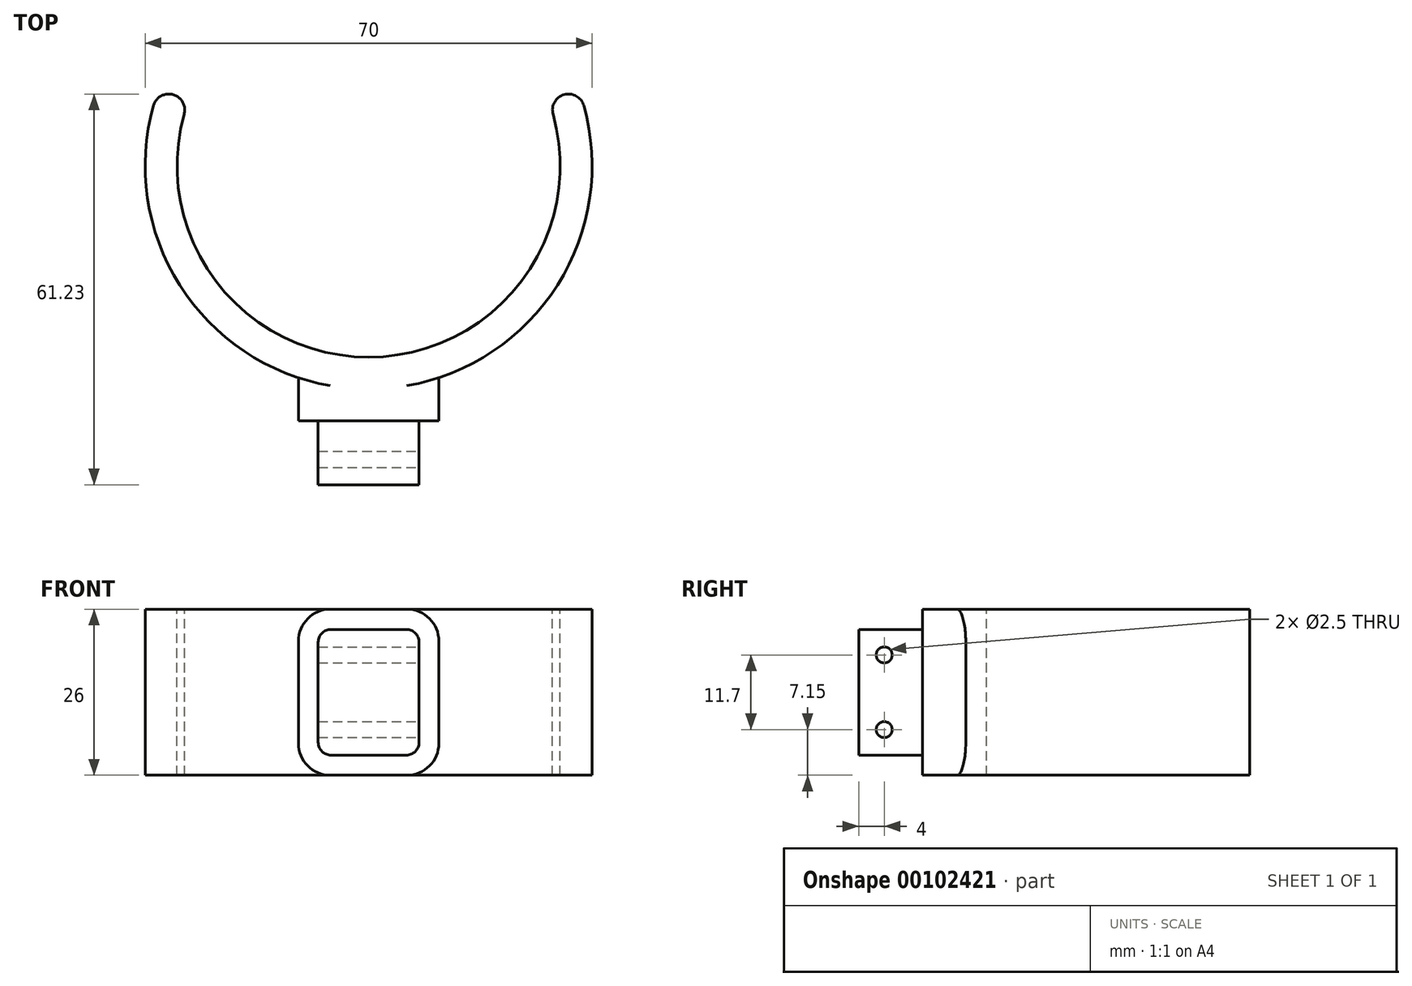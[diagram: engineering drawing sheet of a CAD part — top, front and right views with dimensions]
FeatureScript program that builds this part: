
annotation { "Feature Type Name" : "Feature", "Feature Type Description" : "" }
export const myFeature = defineFeature(function(context is Context, id is Id, definition is map)
    precondition{}
    {
        {
            var Q0;
            Q0=qCreatedBy(makeId("Right.planeOp"),FACE);
            var sketch = newSketch(context, id + "F0", { "sketchPlane" : qUnion([Q0])});
            skLineSegment(sketch, "E0.bottom", {"start": v(0, -13) * mm, "end": v(5, -13) * mm});
            skLineSegment(sketch, "E0.top", {"start": v(0, 13) * mm, "end": v(5, 13) * mm});
            skLineSegment(sketch, "E0.left", {"start": v(0, -13) * mm, "end": v(0, 13) * mm});
            skLineSegment(sketch, "E0.right", {"start": v(5, -13) * mm, "end": v(5, 13) * mm});
            skLineSegment(sketch, "E1", {"start": v(35, 60.61) * mm, "end": v(35, -54.9) * mm, "construction": true});
            skSolve(sketch);
        }
        {
            var Q0;
            Q0 = qSketchRegion(id + "F0", true);
            var Q1;
            Q1=sQuery(id+"F0.wireOp",EDGE,"E1");
            revolve(context, id + "F1", {"entities" : qUnion([Q0]), "axis" : qUnion([Q1]), "revolveType" : RevolveType.SYMMETRIC, "angle" : 220 * degree});
        }
        {
            var Q0;
            Q0=qCreatedBy(makeId("Front.planeOp"),FACE);
            var sketch = newSketch(context, id + "F2", { "sketchPlane" : qUnion([Q0])});
            skLineSegment(sketch, "E2.bottom", {"start": v(11, 13) * mm, "end": v(-11, 13) * mm});
            skLineSegment(sketch, "E2.top", {"start": v(11, -13) * mm, "end": v(-11, -13) * mm});
            skLineSegment(sketch, "E2.left", {"start": v(11, 13) * mm, "end": v(11, -13) * mm});
            skLineSegment(sketch, "E2.right", {"start": v(-11, 13) * mm, "end": v(-11, -13) * mm});
            skSolve(sketch);
        }
        {
            var Q0;
            Q0 = qSketchRegion(id + "F2", true);
            extrude(context, id + "F3", {"entities" : qUnion([Q0]), "operationType" : NewBodyOperationType.ADD, "depth" : 5 * mm, "hasSecondDirection" : true, "secondDirectionBound" : SecondDirectionBoundingType.UP_TO_NEXT, "secondDirectionOppositeDirection" : true, "secondDirectionDepth" : 25 * mm});
        }
        {
            var Q0;
            Q0=makeQuery(id+"F1.opRevolve","CAP_EDGE",EDGE,{"disambiguationData":[OSD([sQuery(id+"F0.wireOp",EDGE,"E0.left")])],"isStart":true});
            var Q1;
            Q1=makeQuery(id+"F1.opRevolve","CAP_EDGE",EDGE,{"disambiguationData":[OSD([sQuery(id+"F0.wireOp",EDGE,"E0.right")])],"isStart":true});
            var Q2;
            Q2=makeQuery(id+"F1.opRevolve","CAP_EDGE",EDGE,{"disambiguationData":[OSD([sQuery(id+"F0.wireOp",EDGE,"E0.right")])],"isStart":false});
            var Q3;
            Q3=makeQuery(id+"F1.opRevolve","CAP_EDGE",EDGE,{"disambiguationData":[OSD([sQuery(id+"F0.wireOp",EDGE,"E0.left")])],"isStart":false});
            fillet(context, id + "F4", {"entities" : qUnion([Q0, Q1, Q2, Q3]), "radius" : 2.5 * mm, "tangentPropagation" : true, "allowEdgeOverflow" : false});
        }
        {
            var Q0;
            Q0=makeQuery(id+"F3.opExtrude","CAP_FACE",FACE,{"disambiguationData":[OSD([sQuery(id+"F2.wireOp",EDGE,"E2.bottom"),sQuery(id+"F2.wireOp",EDGE,"E2.top"),sQuery(id+"F2.wireOp",EDGE,"E2.left"),sQuery(id+"F2.wireOp",EDGE,"E2.right")])],"isStart":false});
            var sketch = newSketch(context, id + "F5", { "sketchPlane" : qUnion([Q0])});
            skLineSegment(sketch, "E3.bottom", {"start": v(-7.9, 9.85) * mm, "end": v(7.9, 9.85) * mm});
            skLineSegment(sketch, "E3.top", {"start": v(-7.9, -9.85) * mm, "end": v(7.9, -9.85) * mm});
            skLineSegment(sketch, "E3.left", {"start": v(-7.9, 9.85) * mm, "end": v(-7.9, -9.85) * mm});
            skLineSegment(sketch, "E3.right", {"start": v(7.9, 9.85) * mm, "end": v(7.9, -9.85) * mm});
            skSolve(sketch);
        }
        {
            var Q0;
            Q0 = qSketchRegion(id + "F5", true);
            extrude(context, id + "F6", {"entities" : qUnion([Q0]), "operationType" : NewBodyOperationType.ADD, "depth" : 10 * mm});
        }
        {
            var Q0;
            Q0=makeQuery(id+"F6.opExtrude","SWEPT_FACE",FACE,{"disambiguationData":[OSD([sQuery(id+"F5.wireOp",EDGE,"E3.right")])]});
            var sketch = newSketch(context, id + "F7", { "sketchPlane" : qUnion([Q0])});
            skCircle(sketch, "E4", {"center": v(-11, 5.85) * mm, "radius": 1.25 * mm});
            skCircle(sketch, "E5", {"center": v(-11, -5.85) * mm, "radius": 1.25 * mm});
            skSolve(sketch);
        }
        {
            var Q0;
            Q0 = qSketchRegion(id + "F7", true);
            extrude(context, id + "F8", {"entities" : qUnion([Q0]), "operationType" : NewBodyOperationType.REMOVE, "endBound" : BoundingType.THROUGH_ALL, "oppositeDirection" : true, "depth" : 25 * mm});
        }
        {
            var Q0;
            Q0=makeQuery(id+"F6.opExtrude","SWEPT_EDGE",EDGE,{"disambiguationData":[OSD([sQuery(id+"F5.wireOp",EDGE,"E3.bottom"),sQuery(id+"F5.wireOp",EDGE,"E3.right")])]});
            var Q1;
            Q1=makeQuery(id+"F6.opExtrude","SWEPT_EDGE",EDGE,{"disambiguationData":[OSD([sQuery(id+"F5.wireOp",EDGE,"E3.top"),sQuery(id+"F5.wireOp",EDGE,"E3.right")])]});
            var Q2;
            Q2=makeQuery(id+"F6.opExtrude","SWEPT_EDGE",EDGE,{"disambiguationData":[OSD([sQuery(id+"F5.wireOp",EDGE,"E3.top"),sQuery(id+"F5.wireOp",EDGE,"E3.left")])]});
            var Q3;
            Q3=makeQuery(id+"F6.opExtrude","SWEPT_EDGE",EDGE,{"disambiguationData":[OSD([sQuery(id+"F5.wireOp",EDGE,"E3.bottom"),sQuery(id+"F5.wireOp",EDGE,"E3.left")])]});
            fillet(context, id + "F9", {"entities" : qUnion([Q0, Q1, Q2, Q3]), "radius" : 2 * mm, "tangentPropagation" : true, "allowEdgeOverflow" : false});
        }
        {
            var Q0;
            Q0=makeQuery(id+"F3.opExtrude","SWEPT_EDGE",EDGE,{"disambiguationData":[OSD([sQuery(id+"F2.wireOp",EDGE,"E2.bottom"),sQuery(id+"F2.wireOp",EDGE,"E2.right")])]});
            var Q1;
            Q1=makeQuery(id+"F3.opExtrude","SWEPT_EDGE",EDGE,{"disambiguationData":[OSD([sQuery(id+"F2.wireOp",EDGE,"E2.top"),sQuery(id+"F2.wireOp",EDGE,"E2.right")])]});
            var Q2;
            Q2=makeQuery(id+"F3.opExtrude","SWEPT_EDGE",EDGE,{"disambiguationData":[OSD([sQuery(id+"F2.wireOp",EDGE,"E2.top"),sQuery(id+"F2.wireOp",EDGE,"E2.left")])]});
            var Q3;
            Q3=makeQuery(id+"F3.opExtrude","SWEPT_EDGE",EDGE,{"disambiguationData":[OSD([sQuery(id+"F2.wireOp",EDGE,"E2.bottom"),sQuery(id+"F2.wireOp",EDGE,"E2.left")])]});
            fillet(context, id + "F10", {"entities" : qUnion([Q0, Q1, Q2, Q3]), "radius" : 5 * mm, "tangentPropagation" : true, "allowEdgeOverflow" : false});
        }
    });
